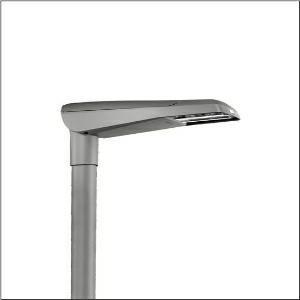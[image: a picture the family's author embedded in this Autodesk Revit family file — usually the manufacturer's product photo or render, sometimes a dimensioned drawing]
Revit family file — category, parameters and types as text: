
# Revit family: streetlight_sl_11_iq_micro___st0_5a_5xc1bc1f08de_0799
name_source: partatom
category: Lighting Fixtures
units: mm (PartAtom-declared; Revit-internal decimal feet)

## family parameters
Cut with Voids When Loaded = No
Host = Face
Light Source = No
Part Type = Normal
Room Calculation Point = No
Round Connector Dimension = Use Diameter
Shared = No

## types (1)
- --- (1 x LED, 3820 lm, 27.4 W, 4000K)
    Apparent Load = 27 VA
    CIE Flux Codes = 42 72 97 100 100
    Color Rendering = 70
    Color Temperature = 4000K
    Default Elevation = 1800 mm
    Description = Streetlight SL 11 iQ micro, mast luminaire, primary light control with 3 zone facetted reflector, of plastic, silver coated, highly specular, primary optical cover: cover, of PMMA, transparent, light distribution: ST0.5a, light emission: direct distribution, primary light characteristic: asymmetric, installation type: post-top, side-entry, lamps: LED, High Power LED, rated values: 3.590lm | 27,7W | 129,6lm/W (begin service life); end service life: 3.590lm | 28,1W; at 50% lumin. flux: 1.795lm | 13,4W | 134lm/W, colour temperature: 2200/2700/3000/4000K, colour rendering: CRI > 70, light colour: 722/727/730/740, light setting 1 begin service life: 100% | 3.590lm | 27,7W | 129,6lm/W | 3.000K, light setting 1 end service life: 28,1W, further light settings possible, control: Street-Remote, Auto-Match, Temp-Guard, Lumen-Switch, Night-Set, Smart-Wire, Light-Fading, Desk-Remote (wireless, voltage-free reading and setting of iQ features in the workshop via application-optimized NFC function/RFID function), optimised constant luminous flux control (CLO 2.0), with cable H07RN-F 3x 1.5mm², mains connection: 220..240V, AC, 50/60Hz, connection cable pre-assembled, cable length: 6,5m, luminaire housing, of diecast aluminium, powder-coated, SITECO metallic grey (DB 702S), please order mast flange separately, inclination adjustable without tools: 0°, 5°, 10°, 15° (post-top) | 0°, -5°, -10°, -15° (side-entry), sealing non-destructively replaceable, multi-level sealing system, length: 600mm, width: 174mm, height: 116mm, mast flange for spigot size: 42mm (side-entry): 5XC10008XM4, 60/48mm (side-entry/post-top): 5XC10108XM2, 76/60mm (side-entry/post-top): 5XC10108XM1, equipment: Power, protection rating (complete): IP66, insulation class (complete): insulation class II (safety insulation), certification: CE, ENEC, ENEC+, VDE, impact resistance: IK10, permissible operating ambient temperature for outdoor applications: -25..+50°C, standard-compliant lighting for roads and squares, Environmental Product Declaration (EPD) tested and certified by an independent institute, packaging unit: 1 piece

Light Distribution: ST0.5a
    Height = 116 mm
    Lamp = 1 x LED
    Lamp Light Flux = 3820 lm
    Lamp Power = 27.4 W
    Lamp count = 1
    Length = 600 mm
    Luminous efficacy = 139 lm/W
    Manufacturer = Siteco
    ModVariant = No
    Model = 5XC1BC1F08DE
    Number of Poles = 1
    OnlyDefault = Yes
    Power Factor = 1
    Product Name = Streetlight SL 11 iQ micro | ST0.5a
    Product group = mast luminaire | pylon top
    ProductGroupID = 6100
    Protection Class = Protection class II
    Protection Degree = IP 66
    RLX_Detail_Level = 1
    RLX_Emergency_Light_Flux = 0 lm
    RLX_Emergency_Type = 0
    RLX_Emergency_Type_DB = No
    RlxData = <blob elided: 59501 chars, md5=0f74d2b4>
    Socket = socket
    Standby Power = 0 W
    System Light Flux = 3820 lm
    System Power = 27 W
    Type Comments = individual setting: luminous flux: 100 % | dim-lin: 254 | 726 mA
    Type Image = l_1006566.jpg
    URL = http://relux.com
    VarID = @adj_048791
    Voltage = 0 V
    Weight = 0.00 kg
    Width = 174 mm

## geometry (parser evidence)
native form markers: Blend x4, Sweep x13
no freeform markers — native parametric forms only
